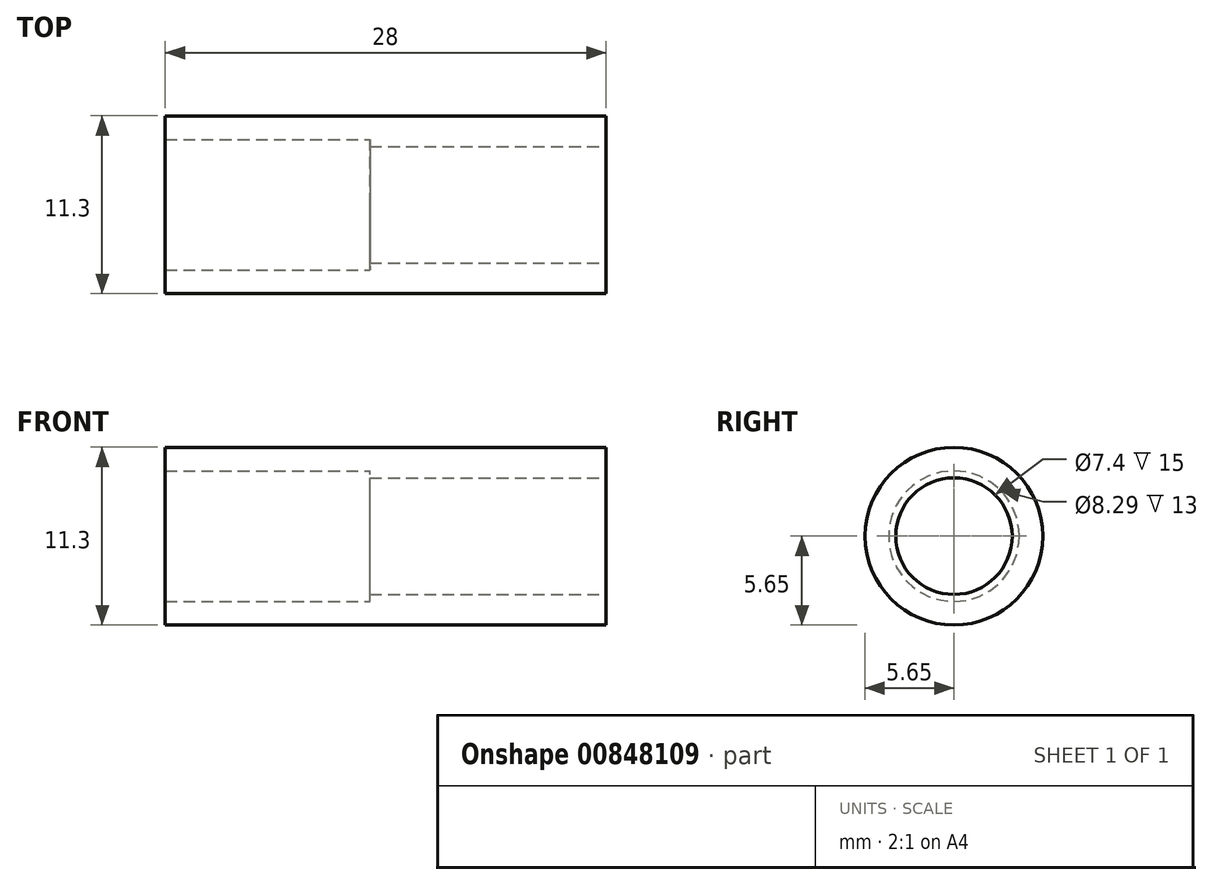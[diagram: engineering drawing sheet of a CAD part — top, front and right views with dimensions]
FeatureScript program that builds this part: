
annotation { "Feature Type Name" : "Feature", "Feature Type Description" : "" }
export const myFeature = defineFeature(function(context is Context, id is Id, definition is map)
    precondition{}
    {
        {
            var Q0;
            Q0=qCreatedBy(makeId("Top.planeOp"),FACE);
            var sketch = newSketch(context, id + "F0", { "sketchPlane" : qUnion([Q0])});
            skLineSegment(sketch, "E0", {"start": v(0, 0) * mm, "end": v(-200, 0) * mm});
            skLineSegment(sketch, "E1", {"start": v(-198, 5.64) * mm, "end": v(-198, 4.14) * mm});
            skLineSegment(sketch, "E2", {"start": v(-198, 4.14) * mm, "end": v(-185, 4.14) * mm});
            skLineSegment(sketch, "E3", {"start": v(-185, 4.14) * mm, "end": v(-185, 0) * mm});
            skLineSegment(sketch, "E4", {"start": v(-185, 0) * mm, "end": v(-170, 0) * mm});
            skLineSegment(sketch, "E5", {"start": v(-170, 0) * mm, "end": v(-170, 5.64) * mm});
            skLineSegment(sketch, "E6", {"start": v(-170, 5.64) * mm, "end": v(-198, 5.64) * mm});
            skLineSegment(sketch, "E7", {"start": v(-185, 3.7) * mm, "end": v(-170, 3.7) * mm});
            skSolve(sketch);
        }
        {
            var Q0;
            Q0=makeQuery(id+"F0.imprint","IMPRINT",FACE,{"disambiguationData":[TD([[makeQuery(id+"F0.imprint","IMPRINT",EDGE,{"derivedFrom":sQuery(id+"F0.wireOp",EDGE,"E1")}),1.0]])]});
            var Q1;
            Q1=sQuery(id+"F0.wireOp",EDGE,"E0");
            revolve(context, id + "F1", {"surfaceOperationType" : NewSurfaceOperationType.NEW, "entities" : qUnion([Q0]), "axis" : qUnion([Q1]), "revolveType" : RevolveType.FULL});
        }
    });
